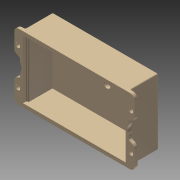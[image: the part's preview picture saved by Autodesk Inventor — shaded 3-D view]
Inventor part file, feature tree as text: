
AUTODESK INVENTOR PART (.ipt)
format: ipt  version: 2015 (Build 190159000, 159)  size: 651,264 bytes
history: native  units: in
note: dims shown in document units (in); Inventor stores cm internally (conversion verified against a paired STEP export)
features: sketch x23, extrude x20, fillet x13, pattern_linear x5, plane x4, projected_geometry x4
ambient origin geometry x8: Origin, YZ Plane, XZ Plane, XY Plane, X Axis, Y Axis, Z Axis, Center Point
bodies: Solid1 (feature_tree)
feature tree (69):
  sketch  "Sketch1"  dims[d7=0.25in d10=4.13in]
  plane  "Work Plane1"
  extrude  "Extrusion2"  Depth=4.13in
  plane  "Work Plane3"
  sketch  "Sketch4"  dims[d22=2.605in d23=1.29in]
  plane  "Work Plane2"
  extrude  "Extrusion8"  Depth=0.075in TaperAngle=0.0deg
  sketch  "Sketch10"  dims[d76=0.3in d77=0.75in d80=0.3in]
  sketch  "Sketch7"  dims[d37=1.6in d55=2.6in d56=1.3in d68=0.15in]
  extrude  "Extrusion6"  Depth=1.29in
  extrude  "Extrusion7"  Depth=0.125in
  fillet  "Fillet5"  Radius=0.125in
  fillet  "Fillet7"  Radius=0.125in
  fillet  "Fillet8"  Radius=2.8in
  extrude  "Extrusion9"  Depth=2.6in
  fillet  "Fillet11"  Radius=1.3in
  fillet  "Fillet12"  Radius=0.15in
  extrude  "Extrusion17"  Depth=0.2in TaperAngle=0.0deg
  fillet  "Fillet15"  Radius=0.15in
  extrude  "Extrusion18"  Depth=0.15in
  fillet  "Fillet16"  Radius=0.265in
  extrude  "Extrusion19"  Depth=0.3in
  fillet  "Fillet17"  Radius=0.3in
  extrude  "Extrusion20"  Depth=0.3in
  fillet  "Fillet18"  Radius=0.75in
  extrude  "Extrusion21"  Depth=0.125in
  plane  "Work Plane4"
  extrude  "Extrusion23"  Depth=0.55in
  extrude  "Extrusion31"  Depth=1.8in
  extrude  "Extrusion33"  Depth=0.25in TaperAngle=0.0deg
  extrude  "Extrusion34"  Depth=0.125in
  fillet  "Fillet25"  Radius=0.4in
  extrude  "Extrusion35"  Depth=0.4in TaperAngle=0.0deg
  fillet  "Fillet26"  Radius=0.75in
  fillet  "Fillet27"  Radius=0.1in
  fillet  "Fillet28"  Radius=0.1in
  extrude  "Extrusion36"  Depth=0.3in TaperAngle=0.0deg
  extrude  "Extrusion37"  Depth=0.025in
  extrude  "Extrusion38"  Depth=2.04in
  pattern_linear  "Rectangular Pattern5"  Spacing1=0.1in  [1 undecoded]
  pattern_linear  "Rectangular Pattern6"  Spacing1=0.25in  [1 undecoded]
  pattern_linear  "Rectangular Pattern7"  Spacing1=0.125in  [1 undecoded]
  pattern_linear  "Rectangular Pattern8"  Spacing1=0.1in  [1 undecoded]
  extrude  "Extrusion39"  Depth=0.3937in
  pattern_linear  "Rectangular Pattern9"  Spacing1=0.125in  [1 undecoded]
  extrude  "Extrusion40"  Depth=0.3937in
  sketch  "Sketch2"  dims[d11=2.0in d20=0.075in d21=0.0in]
  sketch  "Sketch5"  dims[d30=0.125in d31=0.125in d32=0.125in d33=0.125in d36=2.8in]
  sketch  "Sketch8"  dims[d69=0.15in d70=0.2in d71=0.0in d72=0.15in]
  sketch  "Sketch9"  dims[d73=0.265in d74=0.15in d75=0.265in]
  sketch  "Sketch13"  dims[d81=0.75in d82=0.3in d83=0.75in]
  sketch  "Sketch22"  dims[d84=0.2in d85=0.0in d86=0.125in]
  sketch  "Sketch23"  dims[d89=0.55in d90=0.55in]
  sketch  "Sketch24"  dims[d91=3.28in d92=1.8in]
  sketch  "Sketch26"  dims[d95=0.081in d98=0.25in d99=0.0in]
  projected_geometry  "Projected Loop1"
  sketch  "Sketch29"  dims[d100=0.125in d101=0.125in d107=0.4in]
  projected_geometry  "Projected Loop3"
  sketch  "Sketch33"  dims[d108=0.4in d109=0.4in d110=0.0in d117=0.75in d132=0.1in d133=0.1in]
  projected_geometry  "Projected Loop6"
  sketch  "Sketch37"  dims[d149=0.3in d191=0.25in d192=0.0in]
  sketch  "Sketch38"  dims[d193=0.025in d194=0.6102in]
  projected_geometry  "Projected Loop9"
  sketch  "Sketch39"  dims[d195=0.6102in d197=2.04in]
  sketch  "Sketch40"  dims[d198=1.0in d199=0.0in]
  sketch  "Sketch41"  dims[d200=0.025in]
  sketch  "Sketch42"  dims[d201=0.06in]
  sketch  "Sketch43"  dims[d202=0.25in d203=0.0in]
  sketch  "Sketch44"  dims[d204=0.05in d205=0.1in d207=0.25in d208=0.0in d209=0.125in d210=0.1in d211=0.0625in d212=0.125in d213=0.0625in d214=0.275in d215=0.275in d216=0.125in d217=0.1625in d218=0.125in d219=0.125in d220=0.1in d221=0.0in d224=-0.25in d225=0.7in d226=0.0in d244=2.7in d259=0.65in d260=0.0in d263=0.65in d264=0.0in d265=0.1in d266=0.0in d267=0.025in d268=0.15in d269=0.15in d270=0.15in d271=0.3in d272=0.0in d273=0.025in d274=0.025in d275=0.025in d276=0.1in d277=1.7in d279=1.7in d281=0.1in d282=0.29in d283=0.29in d284=0.29in d285=0.2in d286=0.0in d287=0.1in d288=0.05in d289=0.5in d290=0.0in d297=0.05in d298=0.1in d299=0.0in d318=0.3937in d320=1.0in d321=1.1811in d323=0.22in d324=0.3937in d326=1.0in d327=0.7874in d329=1.15in d330=0.3937in d332=1.0in d333=0.7874in d335=1.37in d336=0.3937in d338=1.0in d339=0.7874in d341=1.59in d344=0.1in d345=0.1in d346=0.1in d347=0.1in d348=0.14in d349=0.0in d350=0.7874in d352=3.2in d353=0.3937in d355=1.0in d356=0.1in d357=0.1in d358=0.1in d359=0.1in d360=0.14in d361=0.0in]
note: 5 required parameter values undecoded (feature->parameter linkage not recoverable at this tier; creation-order binding heuristic only, values carry confidence <= 0.55)
